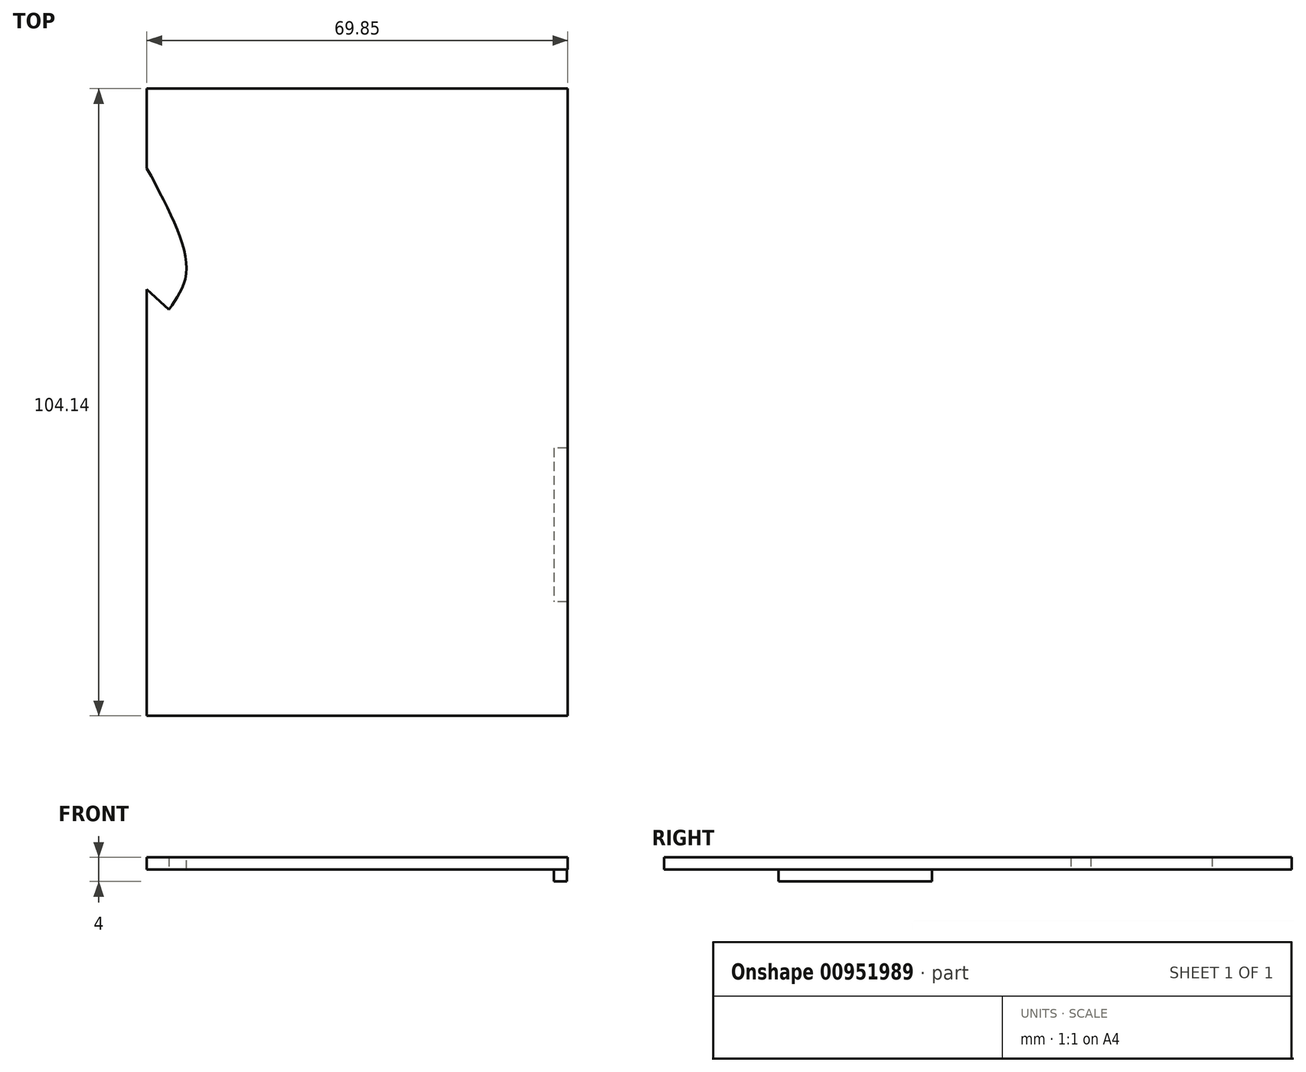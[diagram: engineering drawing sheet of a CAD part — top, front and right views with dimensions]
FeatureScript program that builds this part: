
annotation { "Feature Type Name" : "Feature", "Feature Type Description" : "" }
export const myFeature = defineFeature(function(context is Context, id is Id, definition is map)
    precondition{}
    {
        {
            var Q0;
            Q0=qCreatedBy(makeId("Top.planeOp"),FACE);
            var sketch = newSketch(context, id + "F0", { "sketchPlane" : qUnion([Q0])});
            skLineSegment(sketch, "E0.bottom", {"start": v(-50.47, -3.87) * mm, "end": v(-47.93, -3.87) * mm});
            skLineSegment(sketch, "E0.top", {"start": v(-50.47, -29.27) * mm, "end": v(-47.93, -29.27) * mm});
            skLineSegment(sketch, "E0.left", {"start": v(-50.47, -3.87) * mm, "end": v(-50.47, -29.27) * mm});
            skLineSegment(sketch, "E1.bottom", {"start": v(16.84, -3.87) * mm, "end": v(19.38, -3.87) * mm});
            skLineSegment(sketch, "E1.top", {"start": v(16.84, -29.27) * mm, "end": v(19.38, -29.27) * mm});
            skLineSegment(sketch, "E1.right", {"start": v(19.38, -3.87) * mm, "end": v(19.38, -29.27) * mm});
            skLineSegment(sketch, "E2.top", {"start": v(-28.25, -48.32) * mm, "end": v(-2.85, -48.32) * mm});
            skLineSegment(sketch, "E2.left", {"start": v(-28.25, -45.78) * mm, "end": v(-28.25, -48.32) * mm});
            skLineSegment(sketch, "E2.right", {"start": v(-2.85, -45.78) * mm, "end": v(-2.85, -48.32) * mm});
            skLineSegment(sketch, "E3", {"start": v(-50.47, -29.27) * mm, "end": v(-50.47, -48.32) * mm});
            skLineSegment(sketch, "E4", {"start": v(-50.47, -48.32) * mm, "end": v(-28.25, -48.32) * mm});
            skLineSegment(sketch, "E5", {"start": v(-2.85, -48.32) * mm, "end": v(19.38, -48.32) * mm});
            skLineSegment(sketch, "E6", {"start": v(19.38, -48.32) * mm, "end": v(19.38, -29.27) * mm});
            skLineSegment(sketch, "E7", {"start": v(19.38, -3.87) * mm, "end": v(19.38, 15.18) * mm});
            skLineSegment(sketch, "E8", {"start": v(-50.47, -3.87) * mm, "end": v(-50.47, 15.18) * mm});
            skLineSegment(sketch, "E9", {"start": v(19.38, 15.18) * mm, "end": v(19.38, 55.82) * mm});
            skLineSegment(sketch, "E10", {"start": v(19.38, 55.82) * mm, "end": v(-50.47, 55.82) * mm});
            skLineSegment(sketch, "E11", {"start": v(-50.47, 15.18) * mm, "end": v(-50.47, 22.49) * mm});
            skLineSegment(sketch, "E12", {"start": v(-50.47, 55.82) * mm, "end": v(-50.47, 42.6) * mm});
            skLineSegment(sketch, "E13", {"start": v(-50.47, 22.49) * mm, "end": v(-46.8, 19.15) * mm});
            skFitSpline(sketch, "E14", {"points": [v(-46.8, 19.15) * mm, v(-43.9, 26) * mm, v(-50.47, 42.6) * mm], "startDerivative": vector(10.96, 15.53) * mm, "endDerivative": vector(-16.35, 30.3) * mm});
            skSolve(sketch);
        }
        {
            var Q0;
            Q0 = qSketchRegion(id + "F0", true);
            extrude(context, id + "F1", {"entities" : qUnion([Q0]), "depth" : 2 * mm, "offsetDistance" : 25.4 * mm});
        }
        {
            var Q0;
            Q0=qCreatedBy(makeId("Top.planeOp"),FACE);
            var sketch = newSketch(context, id + "F2", { "sketchPlane" : qUnion([Q0])});
            skLineSegment(sketch, "E15.bottom", {"start": v(19.2, -3.87) * mm, "end": v(17.06, -3.87) * mm});
            skLineSegment(sketch, "E15.top", {"start": v(19.2, -29.35) * mm, "end": v(17.06, -29.35) * mm});
            skLineSegment(sketch, "E15.left", {"start": v(19.2, -3.87) * mm, "end": v(19.2, -29.35) * mm});
            skLineSegment(sketch, "E15.right", {"start": v(17.06, -3.87) * mm, "end": v(17.06, -29.35) * mm});
            skSolve(sketch);
        }
        {
            var Q0;
            Q0 = qSketchRegion(id + "F2", true);
            extrude(context, id + "F3", {"entities" : qUnion([Q0]), "operationType" : NewBodyOperationType.ADD, "oppositeDirection" : true, "depth" : 2 * mm, "offsetDistance" : 25.4 * mm});
        }
    });
